# Revit family: Washer_Milnor_170lb-Capacity_MWF77
name_source: partatom
category: Mechanical Equipment
units: mm (PartAtom-declared; Revit-internal decimal feet)

## family parameters
Always vertical = No
Cut with Voids When Loaded = No
Maintain Annotation Orientation = No
OmniClass Number = 23.45.70.11.14.11
OmniClass Title = Washing Machines
Part Type = Normal
Room Calculation Point = No
Round Connector Dimension = Use Diameter
Shared = No
Work Plane-Based = Yes

## types (2) — shared parameters
Assembly Code = E1010610
Capacity = 170 lb
Construction Details = https://www.arcat.com
Cylinder Depth = 1' - 10"
Cylinder Diameter = 2' - 6"
Default Elevation = 4' - 0"
Description = Milnor Commercial Washer Extractor
Door Base from FF = 2' - 3 3/4"
Door Opening = 1' - 3 1/2"
Door Opening Depth = 1' - 5 3/4"
Dynamic Load = 0.00 kip
Expected Lifespan (Years) = 12
Extraction G-Force = 300 Gs
Frequency = 60 Hz
Green Building-LEED = https://www.arcat.com
Installation-Fabrication = https://www.arcat.com
Keynote = 11110
MEP Amperage = 21 A
Manufacturer = Pellerin Milnor Corp
Manufacturer Fax = 504-468-3094
Manufacturer Website = http://www.milnor.com
Number of Poles = 1
Phase = 3
Product Data = http://www.arcat.com
Product Properties = https://www.arcat.com
Revision = R1_08-2018
Sales Information = http://www.milnor.com
Send Message = http://www.arcat.com
SpecWizard = https://www.arcat.com
Specification = https://www.arcat.com
Suspension Type = Suspended
URL = http://www.milnor.com
Unit Depth = 6' - 5 7/16"
Unit Height = 6' - 8"
Unit Weight = 5400
Unit Width = 4' - 9 5/8"
Voltage_MEP = 45 V
Warranty Duration (Years) = 5
doorgas = 1' - 6"
zero-valued in all types: Cylinder Volume, Maintenance Schedule (Months), Vibration Frequency

## per-type parameters (varying)
| type | 5 Compartment Supply | Standard Soap Chute |
| mwf77jbe2016284d | No | Yes |
| mwf77jbb2014296d | Yes | No |

note: column(s) folded — value = type name in every type: Model

## geometry (parser evidence)
native form markers: Sweep x3
no freeform markers — native parametric forms only
